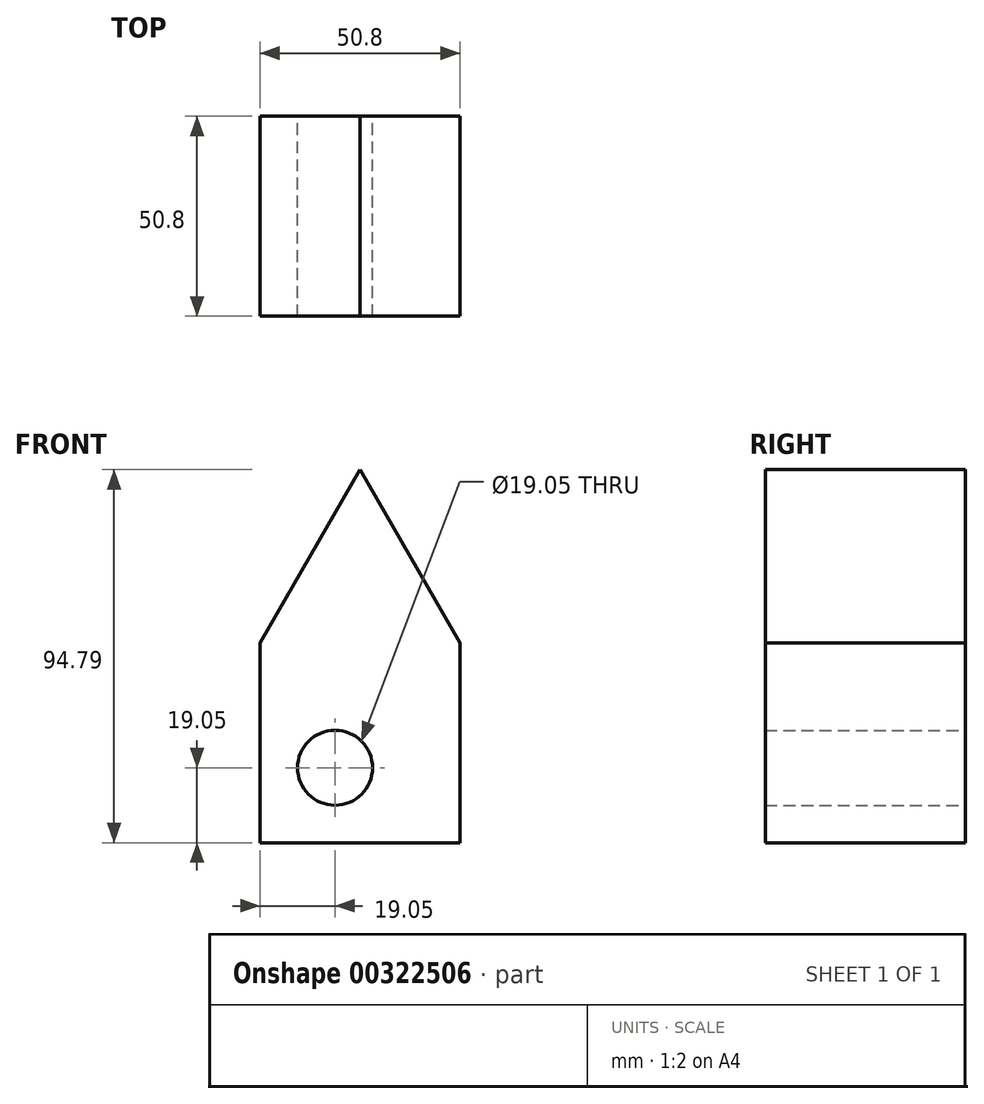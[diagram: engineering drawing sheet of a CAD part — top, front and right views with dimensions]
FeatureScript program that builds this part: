
annotation { "Feature Type Name" : "Feature", "Feature Type Description" : "" }
export const myFeature = defineFeature(function(context is Context, id is Id, definition is map)
    precondition{}
    {
        {
            var Q0;
            Q0=qCreatedBy(makeId("Front.planeOp"),FACE);
            var sketch = newSketch(context, id + "F0", { "sketchPlane" : qUnion([Q0])});
            skLineSegment(sketch, "E0.top", {"start": v(25.4, -25.4) * mm, "end": v(-25.4, -25.4) * mm});
            skLineSegment(sketch, "E0.left", {"start": v(25.4, 25.4) * mm, "end": v(25.4, -25.4) * mm});
            skLineSegment(sketch, "E0.right", {"start": v(-25.4, 25.4) * mm, "end": v(-25.4, -25.4) * mm});
            skLineSegment(sketch, "E1", {"start": v(-25.4, 25.4) * mm, "end": v(0, 69.4) * mm});
            skLineSegment(sketch, "E2", {"start": v(25.4, 25.4) * mm, "end": v(0, 69.4) * mm});
            skCircle(sketch, "E3", {"center": v(-6.35, -6.35) * mm, "radius": 9.53 * mm});
            skSolve(sketch);
        }
        {
            var Q0;
            Q0 = qSketchRegion(id + "F0", true);
            extrude(context, id + "F1", {"entities" : qUnion([Q0]), "depth" : 50.8 * mm});
        }
    });
